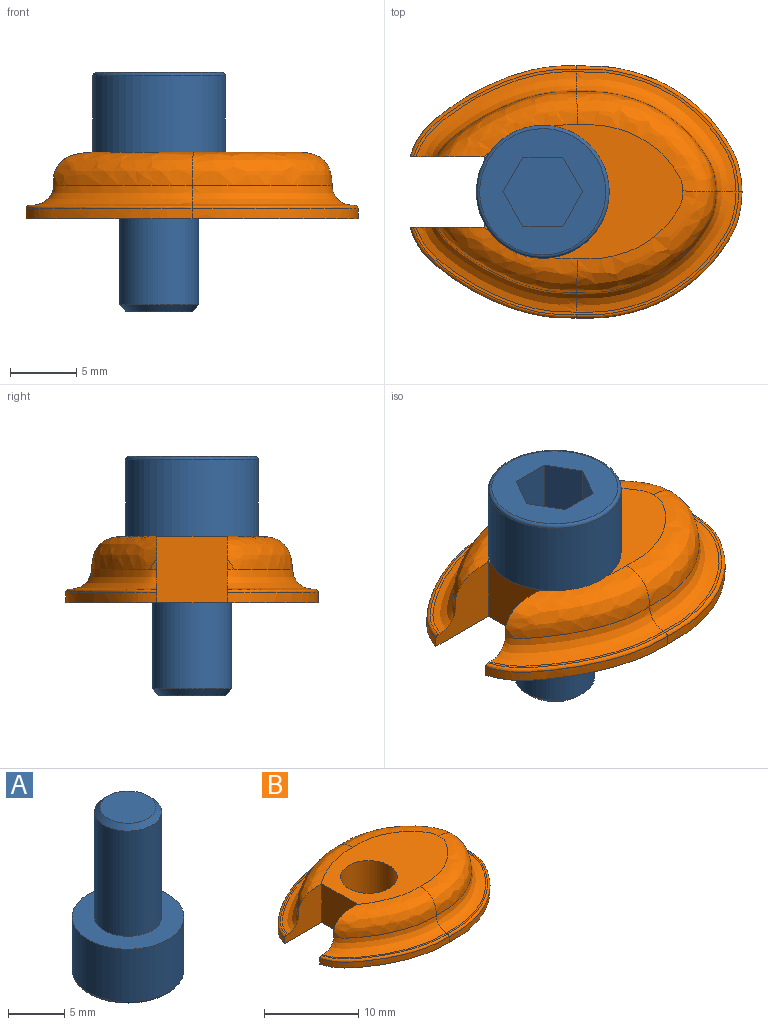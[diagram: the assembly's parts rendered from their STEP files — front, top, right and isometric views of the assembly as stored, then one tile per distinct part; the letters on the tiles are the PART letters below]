
ASSEMBLY  parts=2 mates=1
PART A: 14 faces, bbox 10.8x10.8x18 mm
  f0: plane 10x10mm, normal (0,0,1), area 50.3mm2, adj f1,f3
  f1: cylinder r=5mm len=10mm, axis (0,0,-1), area 180.6mm2, adj f0,f12
  f2: plane 9.5x9.5mm, normal (0,0,-1), area 47.5mm2, adj f5,f6,f7,f8,f9,f10,f12
  f3: cylinder r=3mm len=11.5mm, axis (0,0,-1), area 216.8mm2, adj f0,f13
  f4: plane 5x5mm, normal (0,0,1), area 19.6mm2, adj f13
  f5: plane 4x2.6mm, normal (0.87,-0.5,0), area 12mm2, adj f2,f6,f10,f11
  f6: plane 4x2.6mm, normal (0.87,0.5,0), area 12mm2, adj f2,f5,f7,f11
  f7: plane 4x3mm, normal (0,1,0), area 12mm2, adj f2,f6,f8,f11
  f8: plane 4x2.6mm, normal (-0.87,0.5,0), area 12mm2, adj f2,f7,f9,f11
  f9: plane 4x2.6mm, normal (-0.87,-0.5,0), area 12mm2, adj f2,f8,f10,f11
  f10: plane 4x3mm, normal (0,-1,0), area 12mm2, adj f2,f5,f9,f11
  f11: plane 6x5.2mm, normal (0,0,-1), area 23.4mm2, adj f5,f6,f7,f8,f9,f10
  f12: torus R=4.75mm, axis (0,0,1), area 12.1mm2, adj f1,f2
  f13: cone r=2.5mm half-angle=45deg, axis (0,0,-1), area 12.2mm2, adj f3,f4
PART B: 25 faces, bbox 25.4x19.4x5.3 mm
  f0: plane 24.49x18.51mm, normal (0,0,1), area 12.5mm2, adj f1,f3,f12,f13,f14,f15,f20,f21
  f1: plane 5.86x5.26mm, normal (0,-1,0), area 19mm2, adj f0,f2,f7,f8,f10,f11,f15,f16
  f2: plane 5.3x5mm, normal (-1,0,0), area 26.5mm2, adj f1,f3,f8,f11
  f3: plane 5.86x5.26mm, normal (0,1,0), area 19mm2, adj f0,f2,f4,f8,f9,f11,f12,f19
  f4: extruded ~12.5x6.85mm, area 11.3mm2, adj f3,f5,f8,f23
  f5: extruded ~12.5x9.51mm, area 13mm2, adj f4,f6,f8,f22
  f6: extruded ~12.5x9.51mm, area 13mm2, adj f5,f7,f8,f21
  f7: extruded ~12.5x6.85mm, area 11.3mm2, adj f1,f6,f8,f20
  f8: plane 25x19.03mm, normal (0,0,-1), area 320.5mm2, adj f1,f2,f3,f4,f5,f6,f7,f24
  f9: extruded ~0.79x0.54mm, area 0.3mm2, adj f3,f12,f19
  f10: extruded ~0.79x0.54mm, area 0.3mm2, adj f1,f15,f16
  f11: plane 15.23x10.31mm, normal (0,0,1), area 94.8mm2, adj f1,f2,f3,f16,f17,f18,f19,f24
  f12: bspline ~12.33x7.33mm, area 30.5mm2, adj f0,f3,f9,f13,f19
  f13: bspline ~12.68x11.07mm, area 35.7mm2, adj f0,f12,f14,f18
  f14: bspline ~12.68x11.07mm, area 35.7mm2, adj f0,f13,f15,f17
  f15: bspline ~12.33x7.33mm, area 30.5mm2, adj f0,f1,f10,f14,f16
  f16: bspline ~10.94x5.93mm, area 42.8mm2, adj f1,f10,f11,f15,f17
  f17: bspline ~11.5x7.82mm, area 52.1mm2, adj f11,f14,f16,f18
  f18: bspline ~11x7.82mm, area 52.4mm2, adj f11,f13,f17,f19
  f19: bspline ~10.94x5.93mm, area 42.8mm2, adj f3,f9,f11,f12,f18
  f20: bspline ~15.06x7.51mm, area 5.8mm2, adj f0,f1,f7,f21
  f21: bspline ~12.91x9.66mm, area 6.8mm2, adj f0,f6,f20,f22
  f22: bspline ~12.82x9.91mm, area 6.8mm2, adj f0,f5,f21,f23
  f23: bspline ~12.8x7.32mm, area 5.9mm2, adj f0,f3,f4,f22
  f24: cylinder r=3mm len=6mm, axis (0,0,1), area 94.2mm2, adj f8,f11
PLACE A rot(axis=(1,0,0),180deg) t=(-23.21,11.23,-13.48)mm
PLACE B t=(-10,0,-5)mm
MATE fastened B.f24 <-> A.f1  axis (0,0,1) through (0,0,0)mm
